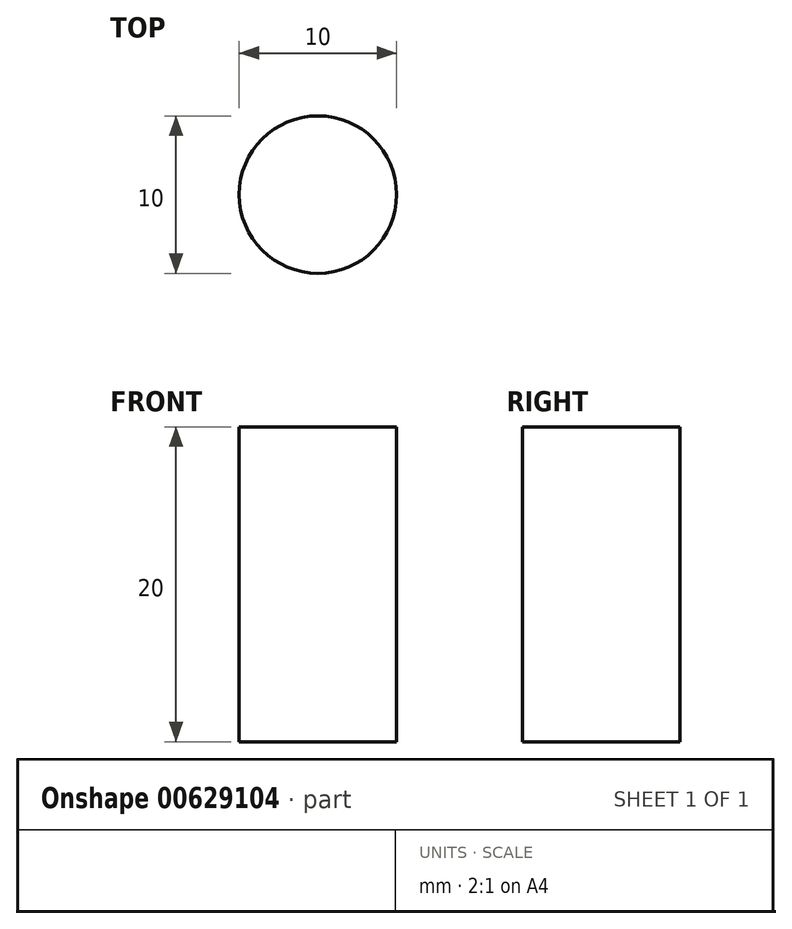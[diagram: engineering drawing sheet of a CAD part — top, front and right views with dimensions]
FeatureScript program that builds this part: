
annotation { "Feature Type Name" : "Feature", "Feature Type Description" : "" }
export const myFeature = defineFeature(function(context is Context, id is Id, definition is map)
    precondition{}
    {
        {
            var Q0;
            Q0=qCreatedBy(makeId("Top.planeOp"),FACE);
            var sketch = newSketch(context, id + "F0", { "sketchPlane" : qUnion([Q0])});
            skCircle(sketch, "E0", {"center": v(0.17, 0) * mm, "radius": 5 * mm});
            skSolve(sketch);
        }
        {
            var Q0;
            Q0 = qSketchRegion(id + "F0", true);
            extrude(context, id + "F1", {"entities" : qUnion([Q0]), "depth" : 20 * mm, "offsetDistance" : 25 * mm, "symmetric" : true});
        }
    });
